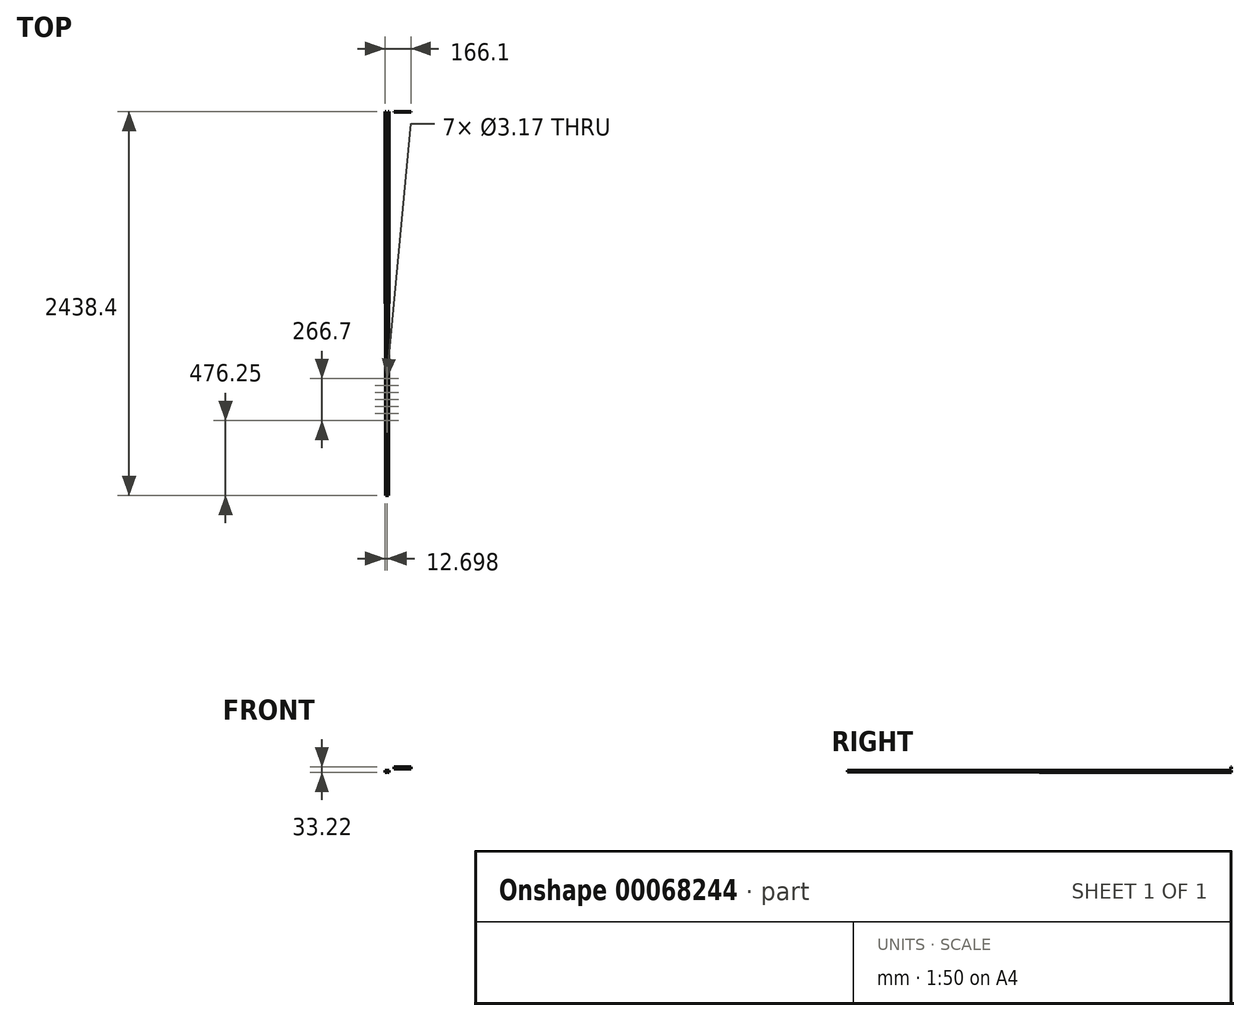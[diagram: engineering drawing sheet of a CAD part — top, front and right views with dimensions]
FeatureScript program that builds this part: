
annotation { "Feature Type Name" : "Feature", "Feature Type Description" : "" }
export const myFeature = defineFeature(function(context is Context, id is Id, definition is map)
    precondition{}
    {
        {
            var Q0;
            Q0=qCreatedBy(makeId("Front.planeOp"),FACE);
            var sketch = newSketch(context, id + "F0", { "sketchPlane" : qUnion([Q0])});
            skLineSegment(sketch, "E0", {"start": v(-47.64, 23.5) * mm, "end": v(-47.64, 20.32) * mm});
            skLineSegment(sketch, "E1", {"start": v(-47.64, 23.5) * mm, "end": v(-54, 23.5) * mm});
            skLineSegment(sketch, "E2", {"start": v(-54, 23.5) * mm, "end": v(-54, 10.8) * mm});
            skLineSegment(sketch, "E3", {"start": v(-54, 10.8) * mm, "end": v(-41.3, 10.8) * mm});
            skLineSegment(sketch, "E4", {"start": v(-41.3, 10.8) * mm, "end": v(-41.3, 13.97) * mm});
            skLineSegment(sketch, "E5", {"start": v(-41.3, 13.97) * mm, "end": v(-50.82, 13.97) * mm});
            skLineSegment(sketch, "E6", {"start": v(-50.82, 13.97) * mm, "end": v(-50.82, 20.32) * mm});
            skLineSegment(sketch, "E7", {"start": v(-50.82, 20.32) * mm, "end": v(-47.64, 20.32) * mm});
            skLineSegment(sketch, "E8", {"start": v(-41.3, 10.8) * mm, "end": v(-41.3, 26.9) * mm, "construction": true});
            skPoint(sketch, "E8.endSnap0", {"position": v(-41.3, 12.38) * mm});
            skLineSegment(sketch, "E9.MirrorCS", {"start": v(-34.94, 23.5) * mm, "end": v(-28.6, 23.5) * mm});
            skLineSegment(sketch, "E10.MirrorCS", {"start": v(-28.6, 23.5) * mm, "end": v(-28.6, 10.8) * mm});
            skLineSegment(sketch, "E11.MirrorCS", {"start": v(-31.77, 13.97) * mm, "end": v(-31.77, 20.32) * mm});
            skLineSegment(sketch, "E12.MirrorCS", {"start": v(-31.77, 20.32) * mm, "end": v(-34.94, 20.32) * mm});
            skLineSegment(sketch, "E13.MirrorCS", {"start": v(-41.3, 13.97) * mm, "end": v(-31.77, 13.97) * mm});
            skLineSegment(sketch, "E14.MirrorCS", {"start": v(-28.6, 10.8) * mm, "end": v(-41.3, 10.8) * mm});
            skLineSegment(sketch, "E15.MirrorCS", {"start": v(-34.94, 23.5) * mm, "end": v(-34.94, 20.32) * mm});
            skSolve(sketch);
        }
        {
            var Q0;
            Q0=makeQuery(id+"F0.imprint","IMPRINT",FACE,{"disambiguationData":[TD([[makeQuery(id+"F0.imprint","IMPRINT",EDGE,{"derivedFrom":sQuery(id+"F0.wireOp",EDGE,"E0")}),-1.0]])]});
            var Q1;
            Q1=makeQuery(id+"F0.imprint","IMPRINT",FACE,{"disambiguationData":[TD([[makeQuery(id+"F0.imprint","IMPRINT",EDGE,{"derivedFrom":sQuery(id+"F0.wireOp",EDGE,"E4")}),-1.0]])]});
            extrude(context, id + "F1", {"entities" : qUnion([Q0, Q1]), "depth" : 1219.2 * mm});
        }
        {
            var Q0;
            Q0=makeQuery(id+"F1.opExtrude","CAP_FACE",FACE,{"disambiguationData":[OSD([sQuery(id+"F0.wireOp",EDGE,"E0"),sQuery(id+"F0.wireOp",EDGE,"E1"),sQuery(id+"F0.wireOp",EDGE,"E2"),sQuery(id+"F0.wireOp",EDGE,"E3"),sQuery(id+"F0.wireOp",EDGE,"E5"),sQuery(id+"F0.wireOp",EDGE,"E6"),sQuery(id+"F0.wireOp",EDGE,"E7"),sQuery(id+"F0.wireOp",EDGE,"E9.MirrorCS"),sQuery(id+"F0.wireOp",EDGE,"E10.MirrorCS"),sQuery(id+"F0.wireOp",EDGE,"E11.MirrorCS"),sQuery(id+"F0.wireOp",EDGE,"E12.MirrorCS"),sQuery(id+"F0.wireOp",EDGE,"E13.MirrorCS"),sQuery(id+"F0.wireOp",EDGE,"E14.MirrorCS"),sQuery(id+"F0.wireOp",EDGE,"E15.MirrorCS")])],"isStart":false});
            var sketch = newSketch(context, id + "F2", { "sketchPlane" : qUnion([Q0])});
            skLineSegment(sketch, "E16.0", {"start": v(-47.64, 23.5) * mm, "end": v(-47.64, 20.32) * mm});
            skLineSegment(sketch, "E16.1", {"start": v(-34.94, 23.5) * mm, "end": v(-34.94, 20.32) * mm});
            skLineSegment(sketch, "E16.2", {"start": v(-31.77, 20.32) * mm, "end": v(-34.94, 20.32) * mm});
            skLineSegment(sketch, "E16.3", {"start": v(-31.77, 13.97) * mm, "end": v(-31.77, 20.32) * mm});
            skLineSegment(sketch, "E16.4", {"start": v(-41.3, 13.97) * mm, "end": v(-31.77, 13.97) * mm});
            skLineSegment(sketch, "E16.5", {"start": v(-41.3, 13.97) * mm, "end": v(-50.82, 13.97) * mm});
            skLineSegment(sketch, "E16.6", {"start": v(-50.82, 13.97) * mm, "end": v(-50.82, 20.32) * mm});
            skLineSegment(sketch, "E16.7", {"start": v(-50.82, 20.32) * mm, "end": v(-47.64, 20.32) * mm});
            skLineSegment(sketch, "E17.0", {"start": v(-34.95, 23.5) * mm, "end": v(-34.95, 20.3) * mm});
            skLineSegment(sketch, "E17.1", {"start": v(-31.78, 20.3) * mm, "end": v(-34.95, 20.3) * mm});
            skLineSegment(sketch, "E17.2", {"start": v(-31.78, 13.98) * mm, "end": v(-31.78, 20.3) * mm});
            skLineSegment(sketch, "E17.3", {"start": v(-41.3, 13.98) * mm, "end": v(-31.78, 13.98) * mm});
            skLineSegment(sketch, "E17.4", {"start": v(-47.63, 23.5) * mm, "end": v(-47.63, 20.3) * mm});
            skLineSegment(sketch, "E17.5", {"start": v(-50.8, 20.3) * mm, "end": v(-47.63, 20.3) * mm});
            skLineSegment(sketch, "E17.6", {"start": v(-50.8, 13.98) * mm, "end": v(-50.8, 20.3) * mm});
            skLineSegment(sketch, "E17.7", {"start": v(-41.3, 13.98) * mm, "end": v(-50.8, 13.98) * mm});
            skLineSegment(sketch, "E18", {"start": v(-47.63, 23.5) * mm, "end": v(-34.95, 23.5) * mm});
            skSolve(sketch);
        }
        {
            var Q0;
            Q0=makeQuery(id+"F2.imprint","IMPRINT",FACE,{"disambiguationData":[TD([[makeQuery(id+"F2.imprint","IMPRINT",EDGE,{"derivedFrom":sQuery(id+"F2.wireOp",EDGE,"E17.0")}),-1.0]])]});
            extrude(context, id + "F3", {"entities" : qUnion([Q0]), "depth" : 1219.2 * mm});
        }
        {
            var Q0;
            Q0=makeQuery(id+"F3.opExtrude","SWEPT_FACE",FACE,{"disambiguationData":[OSD([sQuery(id+"F2.wireOp",EDGE,"E18")])]});
            var sketch = newSketch(context, id + "F4", { "sketchPlane" : qUnion([Q0])});
            skLineSegment(sketch, "E19.0", {"start": v(-47.63, -2438.4) * mm, "end": v(-47.63, -1219.2) * mm});
            skLineSegment(sketch, "E19.1", {"start": v(-34.95, -2438.4) * mm, "end": v(-34.95, -1219.2) * mm});
            skLineSegment(sketch, "E19.2", {"start": v(-47.63, -2438.4) * mm, "end": v(-34.95, -2438.4) * mm});
            skLineSegment(sketch, "E19.3", {"start": v(-47.63, -1219.2) * mm, "end": v(-34.95, -1219.2) * mm});
            skLineSegment(sketch, "E20", {"start": v(-47.63, -1828.8) * mm, "end": v(-34.95, -1828.8) * mm, "construction": true});
            skCircle(sketch, "E21", {"center": v(-41.3, -1828.8) * mm, "radius": 1.59 * mm});
            skCircle(sketch, "E22.0.1.0", {"center": v(-41.3, -1873.25) * mm, "radius": 1.59 * mm});
            skCircle(sketch, "E22.0.2.0", {"center": v(-41.3, -1917.7) * mm, "radius": 1.59 * mm});
            skCircle(sketch, "E22.0.3.0", {"center": v(-41.3, -1962.15) * mm, "radius": 1.59 * mm});
            skLineSegment(sketch, "E22.direction1", {"start": v(-41.3, -1828.8) * mm, "end": v(-15.9, -1828.8) * mm, "construction": true});
            skLineSegment(sketch, "E22.direction2", {"start": v(-41.3, -1828.8) * mm, "end": v(-41.3, -1873.25) * mm, "construction": true});
            skCircle(sketch, "E23.0.1.0", {"center": v(-41.3, -1784.35) * mm, "radius": 1.59 * mm});
            skCircle(sketch, "E23.0.2.0", {"center": v(-41.3, -1739.9) * mm, "radius": 1.59 * mm});
            skCircle(sketch, "E23.0.3.0", {"center": v(-41.3, -1695.45) * mm, "radius": 1.59 * mm});
            skLineSegment(sketch, "E23.direction2", {"start": v(-41.3, -1828.8) * mm, "end": v(-41.3, -1784.35) * mm, "construction": true});
            skSolve(sketch);
        }
        {
            var Q0;
            Q0=makeQuery(id+"F4.imprint","IMPRINT",FACE,{"disambiguationData":[TD([[makeQuery(id+"F4.imprint","IMPRINT",EDGE,{"derivedFrom":sQuery(id+"F4.wireOp",EDGE,"E22.0.3.0")}),1.0]])]});
            var Q1;
            Q1=makeQuery(id+"F4.imprint","IMPRINT",FACE,{"disambiguationData":[TD([[makeQuery(id+"F4.imprint","IMPRINT",EDGE,{"derivedFrom":sQuery(id+"F4.wireOp",EDGE,"E22.0.2.0")}),1.0]])]});
            var Q2;
            Q2=makeQuery(id+"F4.imprint","IMPRINT",FACE,{"disambiguationData":[TD([[makeQuery(id+"F4.imprint","IMPRINT",EDGE,{"derivedFrom":sQuery(id+"F4.wireOp",EDGE,"E22.0.1.0")}),1.0]])]});
            var Q3;
            Q3=makeQuery(id+"F4.imprint","IMPRINT",FACE,{"disambiguationData":[TD([[makeQuery(id+"F4.imprint","IMPRINT",EDGE,{"derivedFrom":sQuery(id+"F4.wireOp",EDGE,"E21")}),1.0]])]});
            var Q4;
            Q4=makeQuery(id+"F4.imprint","IMPRINT",FACE,{"disambiguationData":[TD([[makeQuery(id+"F4.imprint","IMPRINT",EDGE,{"derivedFrom":sQuery(id+"F4.wireOp",EDGE,"E23.0.1.0")}),1.0]])]});
            var Q5;
            Q5=makeQuery(id+"F4.imprint","IMPRINT",FACE,{"disambiguationData":[TD([[makeQuery(id+"F4.imprint","IMPRINT",EDGE,{"derivedFrom":sQuery(id+"F4.wireOp",EDGE,"E23.0.2.0")}),1.0]])]});
            var Q6;
            Q6=makeQuery(id+"F4.imprint","IMPRINT",FACE,{"disambiguationData":[TD([[makeQuery(id+"F4.imprint","IMPRINT",EDGE,{"derivedFrom":sQuery(id+"F4.wireOp",EDGE,"E23.0.3.0")}),1.0]])]});
            extrude(context, id + "F5", {"entities" : qUnion([Q0, Q1, Q2, Q3, Q4, Q5, Q6]), "operationType" : NewBodyOperationType.REMOVE, "endBound" : BoundingType.THROUGH_ALL, "oppositeDirection" : true, "depth" : 25.4 * mm});
        }
        {
            var Q0;
            Q0=makeQuery(id+"F1.opExtrude","SWEPT_FACE",FACE,{"disambiguationData":[OSD([sQuery(id+"F0.wireOp",EDGE,"E5"),sQuery(id+"F0.wireOp",EDGE,"E13.MirrorCS")])]});
            var sketch = newSketch(context, id + "F6", { "sketchPlane" : qUnion([Q0])});
            skLineSegment(sketch, "E24.0", {"start": v(-47.64, -1219.2) * mm, "end": v(-47.64, 0) * mm});
            skLineSegment(sketch, "E24.1", {"start": v(-34.94, -1219.2) * mm, "end": v(-34.94, 0) * mm});
            skLineSegment(sketch, "E24.2", {"start": v(-47.63, -1219.2) * mm, "end": v(-34.95, -1219.2) * mm});
            skLineSegment(sketch, "E25", {"start": v(-47.64, -609.6) * mm, "end": v(-34.94, -609.6) * mm, "construction": true});
            skCircle(sketch, "E26", {"center": v(-41.3, -609.6) * mm, "radius": 1.59 * mm});
            skCircle(sketch, "E27.0.1.0", {"center": v(-41.3, -654.05) * mm, "radius": 1.59 * mm});
            skCircle(sketch, "E27.0.2.0", {"center": v(-41.3, -698.5) * mm, "radius": 1.59 * mm});
            skCircle(sketch, "E27.0.3.0", {"center": v(-41.3, -742.95) * mm, "radius": 1.59 * mm});
            skLineSegment(sketch, "E27.direction1", {"start": v(-41.3, -609.6) * mm, "end": v(-15.9, -609.6) * mm, "construction": true});
            skLineSegment(sketch, "E27.direction2", {"start": v(-41.3, -609.6) * mm, "end": v(-41.3, -654.05) * mm, "construction": true});
            skCircle(sketch, "E28.MirrorC", {"center": v(-41.3, -565.15) * mm, "radius": 1.59 * mm});
            skCircle(sketch, "E29.MirrorC", {"center": v(-41.3, -520.7) * mm, "radius": 1.59 * mm});
            skCircle(sketch, "E30.MirrorC", {"center": v(-41.3, -476.25) * mm, "radius": 1.59 * mm});
            skCircle(sketch, "E31.0.0.4", {"center": v(-41.3, -787.4) * mm, "radius": 1.59 * mm});
            skCircle(sketch, "E31.0.0.5", {"center": v(-41.3, -831.85) * mm, "radius": 1.59 * mm});
            skCircle(sketch, "E31.0.0.6", {"center": v(-41.3, -876.3) * mm, "radius": 1.59 * mm});
            skCircle(sketch, "E31.0.0.7", {"center": v(-41.3, -920.75) * mm, "radius": 1.59 * mm});
            skCircle(sketch, "E31.0.0.8", {"center": v(-41.3, -965.2) * mm, "radius": 1.59 * mm});
            skCircle(sketch, "E31.0.0.9", {"center": v(-41.3, -1009.65) * mm, "radius": 1.59 * mm});
            skCircle(sketch, "E32.0.0.10", {"center": v(-41.3, -1054.1) * mm, "radius": 1.59 * mm});
            skCircle(sketch, "E32.0.0.11", {"center": v(-41.3, -1098.55) * mm, "radius": 1.59 * mm});
            skCircle(sketch, "E32.0.0.12", {"center": v(-41.3, -1143) * mm, "radius": 1.59 * mm});
            skCircle(sketch, "E32.0.0.13", {"center": v(-41.3, -1187.45) * mm, "radius": 1.59 * mm});
            skCircle(sketch, "E33.MirrorC", {"center": v(-41.3, -31.75) * mm, "radius": 1.59 * mm});
            skCircle(sketch, "E34.MirrorC", {"center": v(-41.3, -76.2) * mm, "radius": 1.59 * mm});
            skCircle(sketch, "E35.MirrorC", {"center": v(-41.3, -120.65) * mm, "radius": 1.59 * mm});
            skCircle(sketch, "E36.MirrorC", {"center": v(-41.3, -165.1) * mm, "radius": 1.59 * mm});
            skCircle(sketch, "E37.MirrorC", {"center": v(-41.3, -209.55) * mm, "radius": 1.59 * mm});
            skCircle(sketch, "E38.MirrorC", {"center": v(-41.3, -254) * mm, "radius": 1.59 * mm});
            skCircle(sketch, "E39.MirrorC", {"center": v(-41.3, -298.45) * mm, "radius": 1.59 * mm});
            skCircle(sketch, "E40.MirrorC", {"center": v(-41.3, -342.9) * mm, "radius": 1.59 * mm});
            skCircle(sketch, "E41.MirrorC", {"center": v(-41.3, -387.35) * mm, "radius": 1.59 * mm});
            skCircle(sketch, "E42.MirrorC", {"center": v(-41.3, -431.8) * mm, "radius": 1.59 * mm});
            skSolve(sketch);
        }
        {
            var Q0;
            Q0=makeQuery(id+"F6.imprint","IMPRINT",FACE,{"disambiguationData":[TD([[makeQuery(id+"F6.imprint","IMPRINT",EDGE,{"derivedFrom":sQuery(id+"F6.wireOp",EDGE,"E27.0.3.0")}),1.0]])]});
            var Q1;
            Q1=makeQuery(id+"F6.imprint","IMPRINT",FACE,{"disambiguationData":[TD([[makeQuery(id+"F6.imprint","IMPRINT",EDGE,{"derivedFrom":sQuery(id+"F6.wireOp",EDGE,"E27.0.2.0")}),1.0]])]});
            var Q2;
            Q2=makeQuery(id+"F6.imprint","IMPRINT",FACE,{"disambiguationData":[TD([[makeQuery(id+"F6.imprint","IMPRINT",EDGE,{"derivedFrom":sQuery(id+"F6.wireOp",EDGE,"E27.0.1.0")}),1.0]])]});
            var Q3;
            Q3=makeQuery(id+"F6.imprint","IMPRINT",FACE,{"disambiguationData":[TD([[makeQuery(id+"F6.imprint","IMPRINT",EDGE,{"derivedFrom":sQuery(id+"F6.wireOp",EDGE,"E26")}),1.0]])]});
            var Q4;
            Q4=makeQuery(id+"F6.imprint","IMPRINT",FACE,{"disambiguationData":[TD([[makeQuery(id+"F6.imprint","IMPRINT",EDGE,{"derivedFrom":sQuery(id+"F6.wireOp",EDGE,"E28.MirrorC")}),-1.0]])]});
            var Q5;
            Q5=makeQuery(id+"F6.imprint","IMPRINT",FACE,{"disambiguationData":[TD([[makeQuery(id+"F6.imprint","IMPRINT",EDGE,{"derivedFrom":sQuery(id+"F6.wireOp",EDGE,"E29.MirrorC")}),-1.0]])]});
            var Q6;
            Q6=makeQuery(id+"F6.imprint","IMPRINT",FACE,{"disambiguationData":[TD([[makeQuery(id+"F6.imprint","IMPRINT",EDGE,{"derivedFrom":sQuery(id+"F6.wireOp",EDGE,"E30.MirrorC")}),-1.0]])]});
            var Q7;
            Q7=makeQuery(id+"F6.imprint","IMPRINT",FACE,{"disambiguationData":[TD([[makeQuery(id+"F6.imprint","IMPRINT",EDGE,{"derivedFrom":sQuery(id+"F6.wireOp",EDGE,"E31.0.0.4")}),1.0]])]});
            var Q8;
            Q8=makeQuery(id+"F6.imprint","IMPRINT",FACE,{"disambiguationData":[TD([[makeQuery(id+"F6.imprint","IMPRINT",EDGE,{"derivedFrom":sQuery(id+"F6.wireOp",EDGE,"E31.0.0.5")}),1.0]])]});
            var Q9;
            Q9=makeQuery(id+"F6.imprint","IMPRINT",FACE,{"disambiguationData":[TD([[makeQuery(id+"F6.imprint","IMPRINT",EDGE,{"derivedFrom":sQuery(id+"F6.wireOp",EDGE,"E31.0.0.6")}),1.0]])]});
            var Q10;
            Q10=makeQuery(id+"F6.imprint","IMPRINT",FACE,{"disambiguationData":[TD([[makeQuery(id+"F6.imprint","IMPRINT",EDGE,{"derivedFrom":sQuery(id+"F6.wireOp",EDGE,"E31.0.0.7")}),1.0]])]});
            var Q11;
            Q11=makeQuery(id+"F6.imprint","IMPRINT",FACE,{"disambiguationData":[TD([[makeQuery(id+"F6.imprint","IMPRINT",EDGE,{"derivedFrom":sQuery(id+"F6.wireOp",EDGE,"E31.0.0.8")}),1.0]])]});
            var Q12;
            Q12=makeQuery(id+"F6.imprint","IMPRINT",FACE,{"disambiguationData":[TD([[makeQuery(id+"F6.imprint","IMPRINT",EDGE,{"derivedFrom":sQuery(id+"F6.wireOp",EDGE,"E31.0.0.9")}),1.0]])]});
            var Q13;
            Q13=makeQuery(id+"F6.imprint","IMPRINT",FACE,{"disambiguationData":[TD([[makeQuery(id+"F6.imprint","IMPRINT",EDGE,{"derivedFrom":sQuery(id+"F6.wireOp",EDGE,"E32.0.0.10")}),1.0]])]});
            var Q14;
            Q14=makeQuery(id+"F6.imprint","IMPRINT",FACE,{"disambiguationData":[TD([[makeQuery(id+"F6.imprint","IMPRINT",EDGE,{"derivedFrom":sQuery(id+"F6.wireOp",EDGE,"E32.0.0.11")}),1.0]])]});
            var Q15;
            Q15=makeQuery(id+"F6.imprint","IMPRINT",FACE,{"disambiguationData":[TD([[makeQuery(id+"F6.imprint","IMPRINT",EDGE,{"derivedFrom":sQuery(id+"F6.wireOp",EDGE,"E32.0.0.12")}),1.0]])]});
            var Q16;
            Q16=makeQuery(id+"F6.imprint","IMPRINT",FACE,{"disambiguationData":[TD([[makeQuery(id+"F6.imprint","IMPRINT",EDGE,{"derivedFrom":sQuery(id+"F6.wireOp",EDGE,"E32.0.0.13")}),1.0]])]});
            var Q17;
            Q17=makeQuery(id+"F6.imprint","IMPRINT",FACE,{"disambiguationData":[TD([[makeQuery(id+"F6.imprint","IMPRINT",EDGE,{"derivedFrom":sQuery(id+"F6.wireOp",EDGE,"E42.MirrorC")}),-1.0]])]});
            var Q18;
            Q18=makeQuery(id+"F6.imprint","IMPRINT",FACE,{"disambiguationData":[TD([[makeQuery(id+"F6.imprint","IMPRINT",EDGE,{"derivedFrom":sQuery(id+"F6.wireOp",EDGE,"E41.MirrorC")}),-1.0]])]});
            var Q19;
            Q19=makeQuery(id+"F6.imprint","IMPRINT",FACE,{"disambiguationData":[TD([[makeQuery(id+"F6.imprint","IMPRINT",EDGE,{"derivedFrom":sQuery(id+"F6.wireOp",EDGE,"E40.MirrorC")}),-1.0]])]});
            var Q20;
            Q20=makeQuery(id+"F6.imprint","IMPRINT",FACE,{"disambiguationData":[TD([[makeQuery(id+"F6.imprint","IMPRINT",EDGE,{"derivedFrom":sQuery(id+"F6.wireOp",EDGE,"E39.MirrorC")}),-1.0]])]});
            var Q21;
            Q21=makeQuery(id+"F6.imprint","IMPRINT",FACE,{"disambiguationData":[TD([[makeQuery(id+"F6.imprint","IMPRINT",EDGE,{"derivedFrom":sQuery(id+"F6.wireOp",EDGE,"E38.MirrorC")}),-1.0]])]});
            var Q22;
            Q22=makeQuery(id+"F6.imprint","IMPRINT",FACE,{"disambiguationData":[TD([[makeQuery(id+"F6.imprint","IMPRINT",EDGE,{"derivedFrom":sQuery(id+"F6.wireOp",EDGE,"E37.MirrorC")}),-1.0]])]});
            var Q23;
            Q23=makeQuery(id+"F6.imprint","IMPRINT",FACE,{"disambiguationData":[TD([[makeQuery(id+"F6.imprint","IMPRINT",EDGE,{"derivedFrom":sQuery(id+"F6.wireOp",EDGE,"E36.MirrorC")}),-1.0]])]});
            var Q24;
            Q24=makeQuery(id+"F6.imprint","IMPRINT",FACE,{"disambiguationData":[TD([[makeQuery(id+"F6.imprint","IMPRINT",EDGE,{"derivedFrom":sQuery(id+"F6.wireOp",EDGE,"E35.MirrorC")}),-1.0]])]});
            var Q25;
            Q25=makeQuery(id+"F6.imprint","IMPRINT",FACE,{"disambiguationData":[TD([[makeQuery(id+"F6.imprint","IMPRINT",EDGE,{"derivedFrom":sQuery(id+"F6.wireOp",EDGE,"E34.MirrorC")}),-1.0]])]});
            var Q26;
            Q26=makeQuery(id+"F6.imprint","IMPRINT",FACE,{"disambiguationData":[TD([[makeQuery(id+"F6.imprint","IMPRINT",EDGE,{"derivedFrom":sQuery(id+"F6.wireOp",EDGE,"E33.MirrorC")}),-1.0]])]});
            extrude(context, id + "F7", {"entities" : qUnion([Q0, Q1, Q2, Q3, Q4, Q5, Q6, Q7, Q8, Q9, Q10, Q11, Q12, Q13, Q14, Q15, Q16, Q17, Q18, Q19, Q20, Q21, Q22, Q23, Q24, Q25, Q26]), "operationType" : NewBodyOperationType.REMOVE, "endBound" : BoundingType.THROUGH_ALL, "oppositeDirection" : true, "depth" : 25.4 * mm});
        }
        {
            var Q0;
            Q0=makeQuery(id+"F7.boolean.opBoolean","COPY",EDGE,{"derivedFrom":makeQuery(id+"F7.opExtrude","CAP_EDGE",EDGE,{"disambiguationData":[OSD([sQuery(id+"F6.wireOp",EDGE,"E27.0.3.0")])],"isStart":true})});
            var Q1;
            Q1=makeQuery(id+"F7.boolean.opBoolean","COPY",EDGE,{"derivedFrom":makeQuery(id+"F7.opExtrude","CAP_EDGE",EDGE,{"disambiguationData":[OSD([sQuery(id+"F6.wireOp",EDGE,"E27.0.2.0")])],"isStart":true})});
            var Q2;
            Q2=makeQuery(id+"F7.boolean.opBoolean","COPY",EDGE,{"derivedFrom":makeQuery(id+"F7.opExtrude","CAP_EDGE",EDGE,{"disambiguationData":[OSD([sQuery(id+"F6.wireOp",EDGE,"E27.0.1.0")])],"isStart":true})});
            var Q3;
            Q3=makeQuery(id+"F7.boolean.opBoolean","COPY",EDGE,{"derivedFrom":makeQuery(id+"F7.opExtrude","CAP_EDGE",EDGE,{"disambiguationData":[OSD([sQuery(id+"F6.wireOp",EDGE,"E26")])],"isStart":true})});
            var Q4;
            Q4=makeQuery(id+"F7.boolean.opBoolean","COPY",EDGE,{"derivedFrom":makeQuery(id+"F7.opExtrude","CAP_EDGE",EDGE,{"disambiguationData":[OSD([sQuery(id+"F6.wireOp",EDGE,"E28.MirrorC")])],"isStart":true})});
            var Q5;
            Q5=makeQuery(id+"F7.boolean.opBoolean","COPY",EDGE,{"derivedFrom":makeQuery(id+"F7.opExtrude","CAP_EDGE",EDGE,{"disambiguationData":[OSD([sQuery(id+"F6.wireOp",EDGE,"E29.MirrorC")])],"isStart":true})});
            var Q6;
            Q6=makeQuery(id+"F7.boolean.opBoolean","COPY",EDGE,{"derivedFrom":makeQuery(id+"F7.opExtrude","CAP_EDGE",EDGE,{"disambiguationData":[OSD([sQuery(id+"F6.wireOp",EDGE,"E30.MirrorC")])],"isStart":true})});
            var Q7;
            Q7=makeQuery(id+"F5.boolean.opBoolean","INTERSECT",EDGE,{"derivedFrom":[makeQuery(id+"F3.opExtrude","SWEPT_FACE",FACE,{"disambiguationData":[OSD([sQuery(id+"F2.wireOp",EDGE,"E17.3"),sQuery(id+"F2.wireOp",EDGE,"E17.7")])]}),makeQuery(id+"F5.opExtrude","SWEPT_FACE",FACE,{"disambiguationData":[OSD([sQuery(id+"F4.wireOp",EDGE,"E23.0.3.0")])]})]});
            var Q8;
            Q8=makeQuery(id+"F3.opExtrude","SWEPT_FACE",FACE,{"disambiguationData":[OSD([sQuery(id+"F2.wireOp",EDGE,"E17.3"),sQuery(id+"F2.wireOp",EDGE,"E17.7")])]});
            var Q9;
            Q9=makeQuery(id+"F7.boolean.opBoolean","COPY",EDGE,{"derivedFrom":makeQuery(id+"F7.opExtrude","CAP_EDGE",EDGE,{"disambiguationData":[OSD([sQuery(id+"F6.wireOp",EDGE,"E32.0.0.13")])],"isStart":true})});
            var Q10;
            Q10=makeQuery(id+"F7.boolean.opBoolean","COPY",EDGE,{"derivedFrom":makeQuery(id+"F7.opExtrude","CAP_EDGE",EDGE,{"disambiguationData":[OSD([sQuery(id+"F6.wireOp",EDGE,"E32.0.0.12")])],"isStart":true})});
            var Q11;
            Q11=makeQuery(id+"F7.boolean.opBoolean","COPY",EDGE,{"derivedFrom":makeQuery(id+"F7.opExtrude","CAP_EDGE",EDGE,{"disambiguationData":[OSD([sQuery(id+"F6.wireOp",EDGE,"E32.0.0.11")])],"isStart":true})});
            var Q12;
            Q12=makeQuery(id+"F7.boolean.opBoolean","COPY",EDGE,{"derivedFrom":makeQuery(id+"F7.opExtrude","CAP_EDGE",EDGE,{"disambiguationData":[OSD([sQuery(id+"F6.wireOp",EDGE,"E32.0.0.10")])],"isStart":true})});
            var Q13;
            Q13=makeQuery(id+"F7.boolean.opBoolean","COPY",EDGE,{"derivedFrom":makeQuery(id+"F7.opExtrude","CAP_EDGE",EDGE,{"disambiguationData":[OSD([sQuery(id+"F6.wireOp",EDGE,"E31.0.0.9")])],"isStart":true})});
            var Q14;
            Q14=makeQuery(id+"F7.boolean.opBoolean","COPY",EDGE,{"derivedFrom":makeQuery(id+"F7.opExtrude","CAP_EDGE",EDGE,{"disambiguationData":[OSD([sQuery(id+"F6.wireOp",EDGE,"E31.0.0.8")])],"isStart":true})});
            var Q15;
            Q15=makeQuery(id+"F7.boolean.opBoolean","COPY",EDGE,{"derivedFrom":makeQuery(id+"F7.opExtrude","CAP_EDGE",EDGE,{"disambiguationData":[OSD([sQuery(id+"F6.wireOp",EDGE,"E31.0.0.7")])],"isStart":true})});
            var Q16;
            Q16=makeQuery(id+"F7.boolean.opBoolean","COPY",EDGE,{"derivedFrom":makeQuery(id+"F7.opExtrude","CAP_EDGE",EDGE,{"disambiguationData":[OSD([sQuery(id+"F6.wireOp",EDGE,"E31.0.0.6")])],"isStart":true})});
            var Q17;
            Q17=makeQuery(id+"F7.boolean.opBoolean","COPY",EDGE,{"derivedFrom":makeQuery(id+"F7.opExtrude","CAP_EDGE",EDGE,{"disambiguationData":[OSD([sQuery(id+"F6.wireOp",EDGE,"E31.0.0.5")])],"isStart":true})});
            var Q18;
            Q18=makeQuery(id+"F7.boolean.opBoolean","COPY",EDGE,{"derivedFrom":makeQuery(id+"F7.opExtrude","CAP_EDGE",EDGE,{"disambiguationData":[OSD([sQuery(id+"F6.wireOp",EDGE,"E31.0.0.4")])],"isStart":true})});
            var Q19;
            Q19=makeQuery(id+"F7.boolean.opBoolean","COPY",EDGE,{"derivedFrom":makeQuery(id+"F7.opExtrude","CAP_EDGE",EDGE,{"disambiguationData":[OSD([sQuery(id+"F6.wireOp",EDGE,"E33.MirrorC")])],"isStart":true})});
            var Q20;
            Q20=makeQuery(id+"F7.boolean.opBoolean","COPY",EDGE,{"derivedFrom":makeQuery(id+"F7.opExtrude","CAP_EDGE",EDGE,{"disambiguationData":[OSD([sQuery(id+"F6.wireOp",EDGE,"E34.MirrorC")])],"isStart":true})});
            var Q21;
            Q21=makeQuery(id+"F7.boolean.opBoolean","COPY",EDGE,{"derivedFrom":makeQuery(id+"F7.opExtrude","CAP_EDGE",EDGE,{"disambiguationData":[OSD([sQuery(id+"F6.wireOp",EDGE,"E35.MirrorC")])],"isStart":true})});
            var Q22;
            Q22=makeQuery(id+"F7.boolean.opBoolean","COPY",EDGE,{"derivedFrom":makeQuery(id+"F7.opExtrude","CAP_EDGE",EDGE,{"disambiguationData":[OSD([sQuery(id+"F6.wireOp",EDGE,"E36.MirrorC")])],"isStart":true})});
            var Q23;
            Q23=makeQuery(id+"F7.boolean.opBoolean","COPY",EDGE,{"derivedFrom":makeQuery(id+"F7.opExtrude","CAP_EDGE",EDGE,{"disambiguationData":[OSD([sQuery(id+"F6.wireOp",EDGE,"E37.MirrorC")])],"isStart":true})});
            var Q24;
            Q24=makeQuery(id+"F7.boolean.opBoolean","COPY",EDGE,{"derivedFrom":makeQuery(id+"F7.opExtrude","CAP_EDGE",EDGE,{"disambiguationData":[OSD([sQuery(id+"F6.wireOp",EDGE,"E38.MirrorC")])],"isStart":true})});
            var Q25;
            Q25=makeQuery(id+"F7.boolean.opBoolean","COPY",EDGE,{"derivedFrom":makeQuery(id+"F7.opExtrude","CAP_EDGE",EDGE,{"disambiguationData":[OSD([sQuery(id+"F6.wireOp",EDGE,"E40.MirrorC")])],"isStart":true})});
            var Q26;
            Q26=makeQuery(id+"F7.boolean.opBoolean","COPY",EDGE,{"derivedFrom":makeQuery(id+"F7.opExtrude","CAP_EDGE",EDGE,{"disambiguationData":[OSD([sQuery(id+"F6.wireOp",EDGE,"E39.MirrorC")])],"isStart":true})});
            var Q27;
            Q27=makeQuery(id+"F7.boolean.opBoolean","COPY",EDGE,{"derivedFrom":makeQuery(id+"F7.opExtrude","CAP_EDGE",EDGE,{"disambiguationData":[OSD([sQuery(id+"F6.wireOp",EDGE,"E42.MirrorC")])],"isStart":true})});
            var Q28;
            Q28=makeQuery(id+"F7.boolean.opBoolean","COPY",EDGE,{"derivedFrom":makeQuery(id+"F7.opExtrude","CAP_EDGE",EDGE,{"disambiguationData":[OSD([sQuery(id+"F6.wireOp",EDGE,"E41.MirrorC")])],"isStart":true})});
            chamfer(context, id + "F8", {"entities" : qUnion([Q0, Q1, Q2, Q3, Q4, Q5, Q6, Q7, Q8, Q9, Q10, Q11, Q12, Q13, Q14, Q15, Q16, Q17, Q18, Q19, Q20, Q21, Q22, Q23, Q24, Q25, Q26, Q27, Q28]), "width" : 1.27 * mm, "tangentPropagation" : true});
        }
        {
            var Q0;
            Q0=qCreatedBy(makeId("Front.planeOp"),FACE);
            var sketch = newSketch(context, id + "F9", { "sketchPlane" : qUnion([Q0])});
            skLineSegment(sketch, "E43.bottom", {"start": v(4.16, 44) * mm, "end": v(112.11, 44) * mm});
            skLineSegment(sketch, "E43.top", {"start": v(4.16, 31.3) * mm, "end": v(112.11, 31.3) * mm});
            skLineSegment(sketch, "E43.left", {"start": v(4.16, 44) * mm, "end": v(4.16, 31.3) * mm});
            skLineSegment(sketch, "E43.right", {"start": v(112.11, 44) * mm, "end": v(112.11, 31.3) * mm});
            skSolve(sketch);
        }
        {
            var Q0;
            Q0=makeQuery(id+"F9.imprint","IMPRINT",FACE,{"disambiguationData":[TD([[makeQuery(id+"F9.imprint","IMPRINT",EDGE,{"derivedFrom":sQuery(id+"F9.wireOp",EDGE,"E43.bottom")}),-1.0]])]});
            extrude(context, id + "F10", {"entities" : qUnion([Q0]), "depth" : 3.17 * mm});
        }
    });
